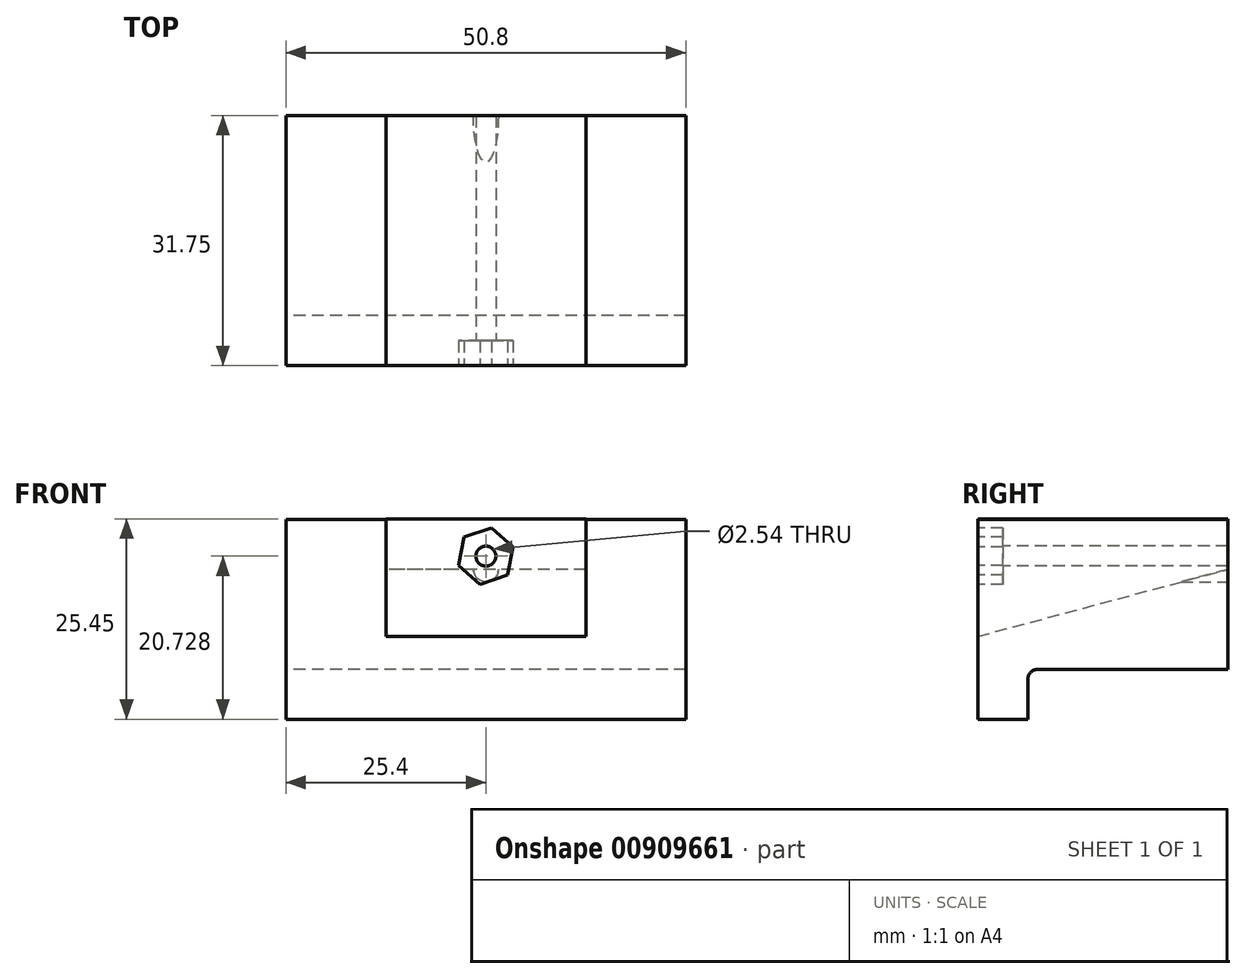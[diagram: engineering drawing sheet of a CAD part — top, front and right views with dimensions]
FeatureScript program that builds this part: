
annotation { "Feature Type Name" : "Feature", "Feature Type Description" : "" }
export const myFeature = defineFeature(function(context is Context, id is Id, definition is map)
    precondition{}
    {
        {
            var Q0;
            Q0=qCreatedBy(makeId("Right.planeOp"),FACE);
            var sketch = newSketch(context, id + "F0", { "sketchPlane" : qUnion([Q0])});
            skLineSegment(sketch, "E0", {"start": v(-5.11, -25.4) * mm, "end": v(1.24, -25.4) * mm});
            skLineSegment(sketch, "E1", {"start": v(1.24, -25.4) * mm, "end": v(1.24, -19.05) * mm});
            skLineSegment(sketch, "E2", {"start": v(1.24, -19.05) * mm, "end": v(26.64, -19.05) * mm});
            skLineSegment(sketch, "E3", {"start": v(26.64, -19.05) * mm, "end": v(26.64, 0) * mm});
            skLineSegment(sketch, "E4", {"start": v(26.64, 0) * mm, "end": v(-5.11, 0) * mm});
            skLineSegment(sketch, "E5", {"start": v(-5.11, 0) * mm, "end": v(-5.11, -25.4) * mm});
            skSolve(sketch);
        }
        {
            var Q0;
            Q0=makeQuery(id+"F0.imprint","IMPRINT",FACE,{"disambiguationData":[TD([[makeQuery(id+"F0.imprint","IMPRINT",EDGE,{"derivedFrom":sQuery(id+"F0.wireOp",EDGE,"E0")}),1.0]])]});
            extrude(context, id + "F1", {"entities" : qUnion([Q0]), "endBound" : BoundingType.SYMMETRIC, "depth" : 50.8 * mm, "offsetDistance" : 25.4 * mm});
        }
        {
            var Q0;
            Q0=qCreatedBy(makeId("Right.planeOp"),FACE);
            var sketch = newSketch(context, id + "F2", { "sketchPlane" : qUnion([Q0])});
            skLineSegment(sketch, "E6", {"start": v(-5.11, 0) * mm, "end": v(26.64, 0) * mm});
            skLineSegment(sketch, "E7", {"start": v(26.64, 0) * mm, "end": v(26.64, -6.35) * mm});
            skLineSegment(sketch, "E8", {"start": v(26.64, -6.35) * mm, "end": v(-5.11, -14.86) * mm});
            skLineSegment(sketch, "E9", {"start": v(-5.11, -14.86) * mm, "end": v(-5.11, 0) * mm});
            skSolve(sketch);
        }
        {
            var Q0;
            Q0 = qSketchRegion(id + "F2", true);
            extrude(context, id + "F3", {"entities" : qUnion([Q0]), "operationType" : NewBodyOperationType.REMOVE, "endBound" : BoundingType.SYMMETRIC, "depth" : 25.4 * mm, "offsetDistance" : 25.4 * mm});
        }
        {
            var Q0;
            Q0=makeQuery(id+"F1.opExtrude","SWEPT_FACE",FACE,{"disambiguationData":[OSD([sQuery(id+"F0.wireOp",EDGE,"E3")])]});
            var sketch = newSketch(context, id + "F4", { "sketchPlane" : qUnion([Q0])});
            skPoint(sketch, "E10", {"position": v(0, -6.35) * mm});
            skSolve(sketch);
        }
        {
            var Q0;
            Q0=sQuery(id+"F4.wireOp",VERTEX,"E10");
            var Q1;
            Q1=makeQuery(id+"F1.opExtrude","SWEPT_BODY",BODY,{"disambiguationData":[OSD([sQuery(id+"F0.wireOp",EDGE,"E0"),sQuery(id+"F0.wireOp",EDGE,"E1"),sQuery(id+"F0.wireOp",EDGE,"E2"),sQuery(id+"F0.wireOp",EDGE,"E3"),sQuery(id+"F0.wireOp",EDGE,"E4"),sQuery(id+"F0.wireOp",EDGE,"E5")])]});
            hole(context, id + "F5", {"style" : HoleStyle.SIMPLE, "endStyle" : HoleEndStyle.THROUGH, "holeDiameter" : 3.17 * mm, "majorDiameter" : 6.35 * mm, "isTappedThrough" : true, "tappedDepth" : 12.7 * mm, "tapClearance" : 3, "locations" : qUnion([Q0]), "scope" : qUnion([Q1])});
        }
        {
            var Q0;
            Q0=qCreatedBy(makeId("Right.planeOp"),FACE);
            var sketch = newSketch(context, id + "F6", { "sketchPlane" : qUnion([Q0])});
            skLineSegment(sketch, "E11", {"start": v(-5.11, -14.86) * mm, "end": v(26.64, -6.35) * mm});
            skLineSegment(sketch, "E12", {"start": v(26.64, -6.35) * mm, "end": v(26.64, 0.05) * mm});
            skLineSegment(sketch, "E13", {"start": v(26.64, 0.05) * mm, "end": v(-5.11, 0.05) * mm});
            skLineSegment(sketch, "E14", {"start": v(-5.11, 0.05) * mm, "end": v(-5.11, -14.86) * mm});
            skSolve(sketch);
        }
        {
            var Q0;
            Q0=makeQuery(id+"F1.opExtrude","SWEPT_EDGE",EDGE,{"disambiguationData":[OSD([sQuery(id+"F0.wireOp",EDGE,"E1"),sQuery(id+"F0.wireOp",EDGE,"E2")])]});
            fillet(context, id + "F7", {"entities" : qUnion([Q0]), "radius" : 1.27 * mm, "tangentPropagation" : true, "allowEdgeOverflow" : false});
        }
        {
            var Q0;
            Q0=makeQuery(id+"F6.imprint","IMPRINT",FACE,{"disambiguationData":[TD([[makeQuery(id+"F6.imprint","IMPRINT",EDGE,{"derivedFrom":sQuery(id+"F6.wireOp",EDGE,"E11")}),1.0]])]});
            extrude(context, id + "F8", {"entities" : qUnion([Q0]), "endBound" : BoundingType.SYMMETRIC, "depth" : 25.4 * mm, "offsetDistance" : 25.4 * mm});
        }
        {
            var Q0;
            Q0=makeQuery(id+"F8.opExtrude","SWEPT_FACE",FACE,{"disambiguationData":[OSD([sQuery(id+"F6.wireOp",EDGE,"E14")])]});
            var sketch = newSketch(context, id + "F9", { "sketchPlane" : qUnion([Q0])});
            skPoint(sketch, "E15", {"position": v(0, -4.67) * mm});
            skSolve(sketch);
        }
        {
            var Q0;
            Q0=sQuery(id+"F9.wireOp",VERTEX,"E15");
            var Q1;
            Q1=makeQuery(id+"F8.opExtrude","SWEPT_BODY",BODY,{"disambiguationData":[OSD([sQuery(id+"F6.wireOp",EDGE,"E11"),sQuery(id+"F6.wireOp",EDGE,"E12"),sQuery(id+"F6.wireOp",EDGE,"E13"),sQuery(id+"F6.wireOp",EDGE,"E14")])]});
            hole(context, id + "F10", {"style" : HoleStyle.SIMPLE, "endStyle" : HoleEndStyle.THROUGH, "holeDiameter" : 2.54 * mm, "majorDiameter" : 6.35 * mm, "isTappedThrough" : true, "tappedDepth" : 12.7 * mm, "tapClearance" : 3, "locations" : qUnion([Q0]), "scope" : qUnion([Q1])});
        }
        {
            var Q0;
            Q0=makeQuery(id+"F8.opExtrude","SWEPT_FACE",FACE,{"disambiguationData":[OSD([sQuery(id+"F6.wireOp",EDGE,"E14")])]});
            var sketch = newSketch(context, id + "F11", { "sketchPlane" : qUnion([Q0])});
            skCircle(sketch, "E16.cCircle", {"center": v(0, -4.67) * mm, "radius": 3.18 * mm, "construction": true});
            skLineSegment(sketch, "E16.0", {"start": v(0.71, -1.08) * mm, "end": v(3.47, -3.5) * mm});
            skLineSegment(sketch, "E16.1", {"start": v(3.47, -3.5) * mm, "end": v(2.76, -7.09) * mm});
            skLineSegment(sketch, "E16.2", {"start": v(2.76, -7.09) * mm, "end": v(-0.71, -8.27) * mm});
            skLineSegment(sketch, "E16.3", {"start": v(-0.71, -8.27) * mm, "end": v(-3.47, -5.85) * mm});
            skLineSegment(sketch, "E16.4", {"start": v(-3.47, -5.85) * mm, "end": v(-2.76, -2.26) * mm});
            skLineSegment(sketch, "E16.5", {"start": v(-2.76, -2.26) * mm, "end": v(0.71, -1.08) * mm});
            skPoint(sketch, "E16.0.midPoint", {"position": v(2.1, -2.28) * mm});
            skSolve(sketch);
        }
        {
            var Q0;
            Q0 = qSketchRegion(id + "F11", true);
            extrude(context, id + "F12", {"entities" : qUnion([Q0]), "operationType" : NewBodyOperationType.REMOVE, "oppositeDirection" : true, "depth" : 3.17 * mm, "offsetDistance" : 25.4 * mm});
        }
    });
